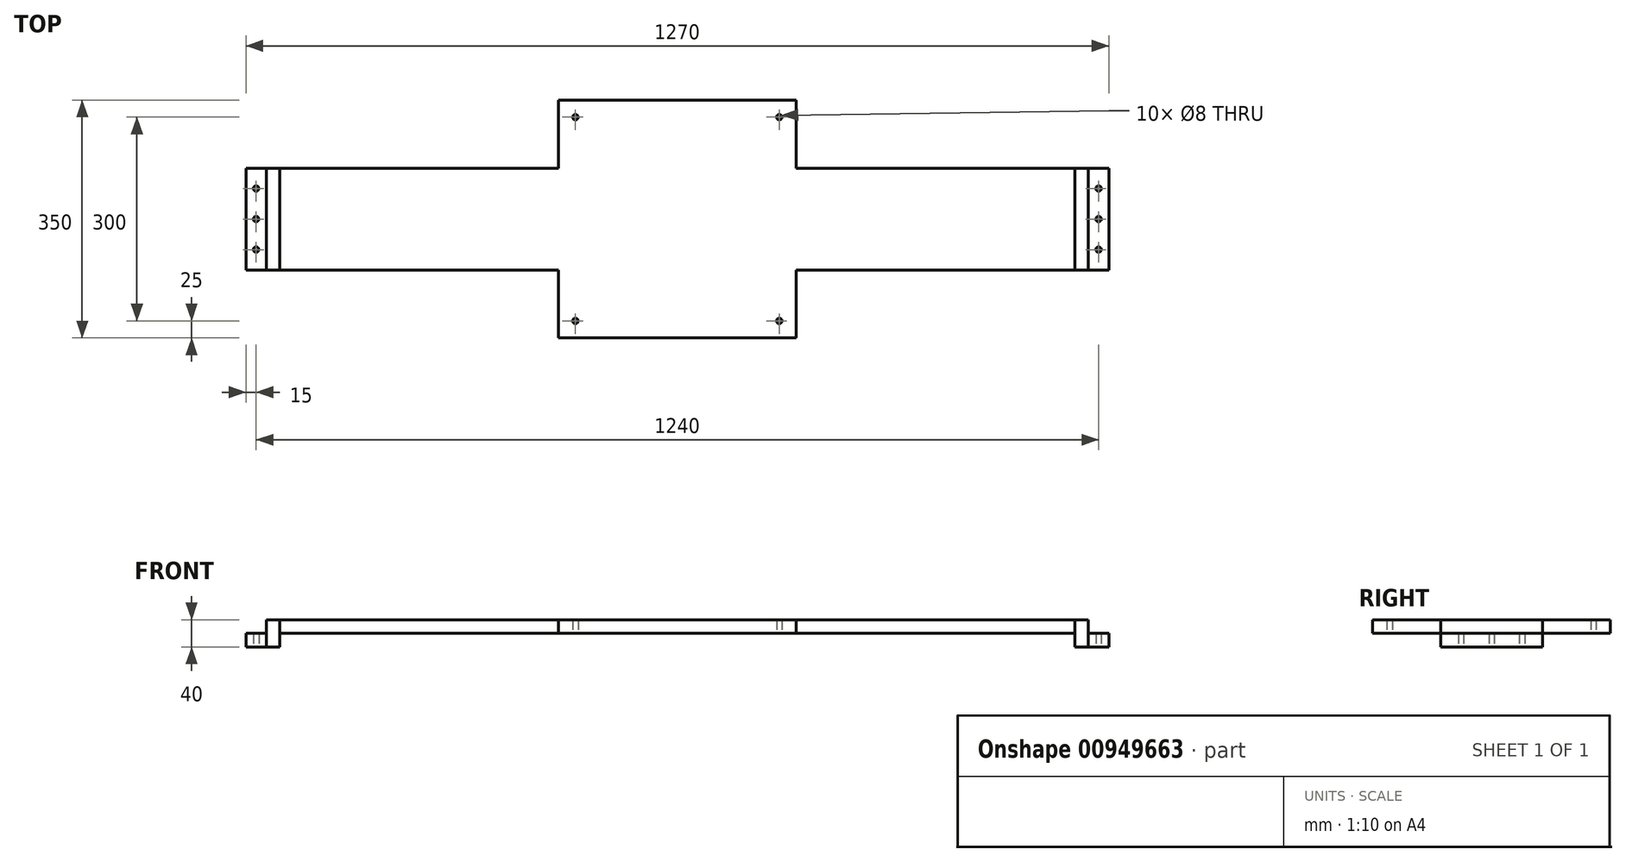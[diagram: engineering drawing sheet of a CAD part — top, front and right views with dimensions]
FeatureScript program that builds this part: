
annotation { "Feature Type Name" : "Feature", "Feature Type Description" : "" }
export const myFeature = defineFeature(function(context is Context, id is Id, definition is map)
    precondition{}
    {
        {
            var Q0;
            Q0=qCreatedBy(makeId("Top.planeOp"),FACE);
            var sketch = newSketch(context, id + "F0", { "sketchPlane" : qUnion([Q0])});
            skLineSegment(sketch, "E0.bottom", {"start": v(150, 150) * mm, "end": v(-150, 150) * mm, "construction": true});
            skLineSegment(sketch, "E0.top", {"start": v(150, -150) * mm, "end": v(-150, -150) * mm, "construction": true});
            skLineSegment(sketch, "E0.left", {"start": v(150, 150) * mm, "end": v(150, -150) * mm, "construction": true});
            skLineSegment(sketch, "E0.right", {"start": v(-150, 150) * mm, "end": v(-150, -150) * mm, "construction": true});
            skPoint(sketch, "E0.middle", {"position": v(0, 0) * mm});
            skCircle(sketch, "E1", {"center": v(-150, 150) * mm, "radius": 4 * mm});
            skCircle(sketch, "E2", {"center": v(150, 150) * mm, "radius": 4 * mm});
            skCircle(sketch, "E3", {"center": v(150, -150) * mm, "radius": 4 * mm});
            skCircle(sketch, "E4", {"center": v(-150, -150) * mm, "radius": 4 * mm});
            skLineSegment(sketch, "E5.bottom", {"start": v(175, 175) * mm, "end": v(-175, 175) * mm});
            skLineSegment(sketch, "E5.top", {"start": v(175, -175) * mm, "end": v(-175, -175) * mm});
            skLineSegment(sketch, "E5.left", {"start": v(175, 175) * mm, "end": v(175, -175) * mm});
            skLineSegment(sketch, "E5.right", {"start": v(-175, 175) * mm, "end": v(-175, -175) * mm});
            skLineSegment(sketch, "E6.bottom", {"start": v(635, 75) * mm, "end": v(-635, 75) * mm});
            skLineSegment(sketch, "E6.top", {"start": v(635, -75) * mm, "end": v(-635, -75) * mm});
            skLineSegment(sketch, "E6.left", {"start": v(635, 75) * mm, "end": v(635, -75) * mm});
            skLineSegment(sketch, "E6.right", {"start": v(-635, 75) * mm, "end": v(-635, -75) * mm});
            skLineSegment(sketch, "E7", {"start": v(605, 75) * mm, "end": v(605, -75) * mm});
            skLineSegment(sketch, "E8", {"start": v(585, 75) * mm, "end": v(585, -75) * mm});
            skLineSegment(sketch, "E9", {"start": v(-605, 75) * mm, "end": v(-605, -75) * mm});
            skLineSegment(sketch, "E10", {"start": v(-585, 75) * mm, "end": v(-585, -75) * mm});
            skLineSegment(sketch, "E11", {"start": v(-620, 75) * mm, "end": v(-620, -75) * mm, "construction": true});
            skLineSegment(sketch, "E12", {"start": v(-635, 0) * mm, "end": v(635, 0) * mm, "construction": true});
            skCircle(sketch, "E13", {"center": v(-620, 0) * mm, "radius": 4 * mm});
            skCircle(sketch, "E14", {"center": v(-620, 45) * mm, "radius": 4 * mm});
            skCircle(sketch, "E15", {"center": v(-620, -45) * mm, "radius": 4 * mm});
            skLineSegment(sketch, "E16", {"start": v(620, 75) * mm, "end": v(620, -75) * mm, "construction": true});
            skCircle(sketch, "E17", {"center": v(620, 0) * mm, "radius": 4 * mm});
            skCircle(sketch, "E18", {"center": v(620, 45) * mm, "radius": 4 * mm});
            skCircle(sketch, "E19", {"center": v(620, -45) * mm, "radius": 4 * mm});
            skSolve(sketch);
        }
        {
            var Q0;
            {var subQ0=sQuery(id+"F0.wireOp",EDGE,"E6.right");Q0=makeQuery(id+"F0.imprint","IMPRINT",FACE,{"disambiguationData":[TD([[makeQuery(id+"F0.imprint","IMPRINT",EDGE,{"derivedFrom":subQ0}),1.0]])]});}
            var Q1;
            {var subQ1=sQuery(id+"F0.wireOp",EDGE,"E6.left");Q1=makeQuery(id+"F0.imprint","IMPRINT",FACE,{"disambiguationData":[TD([[makeQuery(id+"F0.imprint","IMPRINT",EDGE,{"derivedFrom":subQ1}),-1.0]])]});}
            extrude(context, id + "F1", {"entities" : qUnion([Q0, Q1]), "depth" : 20 * mm, "offsetDistance" : 25 * mm});
        }
        {
            var Q0;
            {var subQ0=sQuery(id+"F0.wireOp",EDGE,"E9");Q0=makeQuery(id+"F0.imprint","IMPRINT",FACE,{"disambiguationData":[TD([[makeQuery(id+"F0.imprint","IMPRINT",EDGE,{"derivedFrom":subQ0}),1.0]])]});}
            var Q1;
            {var subQ0=sQuery(id+"F0.wireOp",EDGE,"E7");Q1=makeQuery(id+"F0.imprint","IMPRINT",FACE,{"disambiguationData":[TD([[makeQuery(id+"F0.imprint","IMPRINT",EDGE,{"derivedFrom":subQ0}),-1.0]])]});}
            extrude(context, id + "F2", {"entities" : qUnion([Q0, Q1]), "depth" : 40 * mm, "offsetDistance" : 25 * mm});
        }
        {
            var Q0;
            {var subQ5=sQuery(id+"F0.wireOp",EDGE,"E10");Q0=makeQuery(id+"F0.imprint","IMPRINT",FACE,{"disambiguationData":[TD([[makeQuery(id+"F0.imprint","IMPRINT",EDGE,{"derivedFrom":subQ5}),1.0]])]});}
            var Q1;
            {var subQ0=sQuery(id+"F0.wireOp",EDGE,"E6.bottom");var subQ1=sQuery(id+"F0.wireOp",EDGE,"E5.left");var subQ2=makeQuery(id+"F0.imprint","INTERSECT",VERTEX,{"derivedFrom":[subQ1,subQ0]});Q1=makeQuery(id+"F0.imprint","IMPRINT",FACE,{"disambiguationData":[TD([[makeQuery(id+"F0.imprint","IMPRINT",EDGE,{"disambiguationData":[TD([[subQ2,-1.0]])],"derivedFrom":subQ1}),-1.0]])]});}
            var Q2;
            Q2=makeQuery(id+"F0.imprint","IMPRINT",FACE,{"disambiguationData":[TD([[makeQuery(id+"F0.imprint","IMPRINT",EDGE,{"derivedFrom":sQuery(id+"F0.wireOp",EDGE,"E1")}),-1.0]])]});
            var Q3;
            Q3=makeQuery(id+"F0.imprint","IMPRINT",FACE,{"disambiguationData":[TD([[makeQuery(id+"F0.imprint","IMPRINT",EDGE,{"derivedFrom":sQuery(id+"F0.wireOp",EDGE,"E3")}),-1.0]])]});
            var Q4;
            {var subQ5=sQuery(id+"F0.wireOp",EDGE,"E8");Q4=makeQuery(id+"F0.imprint","IMPRINT",FACE,{"disambiguationData":[TD([[makeQuery(id+"F0.imprint","IMPRINT",EDGE,{"derivedFrom":subQ5}),-1.0]])]});}
            var Q5;
            Q5=makeQuery(id+"F2.opExtrude","CAP_VERTEX",VERTEX,{"disambiguationData":[OSD([sQuery(id+"F0.wireOp",EDGE,"E6.top"),sQuery(id+"F0.wireOp",EDGE,"E10")])],"isStart":false});
            extrude(context, id + "F3", {"entities" : qUnion([Q0, Q1, Q2, Q3, Q4]), "depth" : 40 * mm, "hasOffset" : true, "offsetDistance" : 25 * mm, "hasSecondDirection" : true, "secondDirectionOppositeDirection" : false, "secondDirectionDepth" : 20 * mm, "secondDirectionBoundEntityVertex" : qUnion([Q5])});
        }
    });
